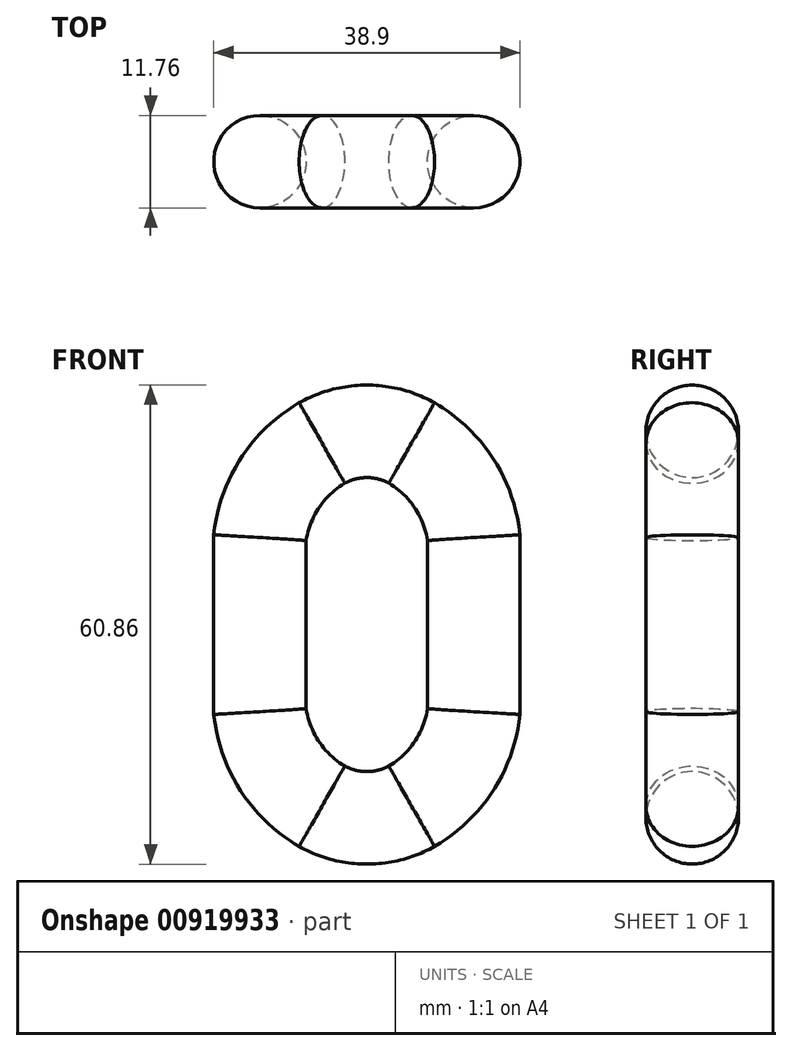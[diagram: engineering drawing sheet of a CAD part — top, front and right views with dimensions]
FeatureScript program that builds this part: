
annotation { "Feature Type Name" : "Feature", "Feature Type Description" : "" }
export const myFeature = defineFeature(function(context is Context, id is Id, definition is map)
    precondition{}
    {
        {
            var Q0;
            Q0=qCreatedBy(makeId("Top.planeOp"),FACE);
            var sketch = newSketch(context, id + "F0", { "sketchPlane" : qUnion([Q0])});
            skCircle(sketch, "E0", {"center": v(13.58, 0) * mm, "radius": 5.88 * mm});
            skSolve(sketch);
        }
        {
            var Q0;
            Q0=qCreatedBy(makeId("Front.planeOp"),FACE);
            var sketch = newSketch(context, id + "F1", { "sketchPlane" : qUnion([Q0])});
            skLineSegment(sketch, "E1", {"start": v(13.58, 0) * mm, "end": v(13.58, 5.5) * mm});
            skArc(sketch, "E2", {"start": v(0, 24.55) * mm, "mid": v(2.94, 24.18) * mm, "end": v(5.7, 23.08) * mm});
            skArc(sketch, "E3", {"start": v(5.7, 23.08) * mm, "mid": v(11.05, 18) * mm, "end": v(13.58, 11.06) * mm});
            skLineSegment(sketch, "E4", {"start": v(13.58, 5.5) * mm, "end": v(13.58, 11.06) * mm});
            skLineSegment(sketch, "E5.MirrorCS", {"start": v(-13.58, 0) * mm, "end": v(-13.58, 5.5) * mm});
            skLineSegment(sketch, "E6.MirrorCS", {"start": v(-13.58, 5.5) * mm, "end": v(-13.58, 11.06) * mm});
            skArc(sketch, "E7.MirrorCS", {"start": v(0, 24.55) * mm, "mid": v(-2.94, 24.18) * mm, "end": v(-5.7, 23.08) * mm});
            skArc(sketch, "E8.MirrorCS", {"start": v(-5.7, 23.08) * mm, "mid": v(-11.05, 18) * mm, "end": v(-13.58, 11.06) * mm});
            skLineSegment(sketch, "E9.MirrorCS", {"start": v(13.58, -5.5) * mm, "end": v(13.58, -11.06) * mm});
            skArc(sketch, "E10.MirrorCS", {"start": v(0, -24.55) * mm, "mid": v(2.94, -24.18) * mm, "end": v(5.7, -23.08) * mm});
            skLineSegment(sketch, "E11.MirrorCS", {"start": v(-13.58, -5.5) * mm, "end": v(-13.58, -11.06) * mm});
            skArc(sketch, "E12.MirrorCS", {"start": v(0, -24.55) * mm, "mid": v(-2.94, -24.18) * mm, "end": v(-5.7, -23.08) * mm});
            skLineSegment(sketch, "E13.MirrorCS", {"start": v(-13.58, 0) * mm, "end": v(-13.58, -5.5) * mm});
            skLineSegment(sketch, "E14.MirrorCS", {"start": v(13.58, 0) * mm, "end": v(13.58, -5.5) * mm});
            skArc(sketch, "E15.MirrorCS", {"start": v(-5.7, -23.08) * mm, "mid": v(-11.05, -18) * mm, "end": v(-13.58, -11.06) * mm});
            skArc(sketch, "E16.MirrorCS", {"start": v(5.7, -23.08) * mm, "mid": v(11.05, -18) * mm, "end": v(13.58, -11.06) * mm});
            skSolve(sketch);
        }
        {
            var Q0;
            Q0=makeQuery(id+"F0.imprint","IMPRINT",FACE,{"disambiguationData":[TD([[makeQuery(id+"F0.imprint","IMPRINT",EDGE,{"derivedFrom":sQuery(id+"F0.wireOp",EDGE,"E0")}),1.0]])]});
            var Q1;
            Q1=sQuery(id+"F1.wireOp",EDGE,"E1");
            var Q2;
            Q2=sQuery(id+"F1.wireOp",EDGE,"E4");
            var Q3;
            Q3=sQuery(id+"F1.wireOp",EDGE,"E3");
            var Q4;
            Q4=sQuery(id+"F1.wireOp",EDGE,"E2");
            var Q5;
            Q5=sQuery(id+"F1.wireOp",EDGE,"E7.MirrorCS");
            var Q6;
            Q6=sQuery(id+"F1.wireOp",EDGE,"E8.MirrorCS");
            var Q7;
            Q7=sQuery(id+"F1.wireOp",EDGE,"E6.MirrorCS");
            var Q8;
            Q8=sQuery(id+"F1.wireOp",EDGE,"E5.MirrorCS");
            var Q9;
            Q9=sQuery(id+"F1.wireOp",EDGE,"E13.MirrorCS");
            var Q10;
            Q10=sQuery(id+"F1.wireOp",EDGE,"E11.MirrorCS");
            var Q11;
            Q11=sQuery(id+"F1.wireOp",EDGE,"E15.MirrorCS");
            var Q12;
            Q12=sQuery(id+"F1.wireOp",EDGE,"E12.MirrorCS");
            var Q13;
            Q13=sQuery(id+"F1.wireOp",EDGE,"E10.MirrorCS");
            var Q14;
            Q14=sQuery(id+"F1.wireOp",EDGE,"E16.MirrorCS");
            var Q15;
            Q15=sQuery(id+"F1.wireOp",EDGE,"E9.MirrorCS");
            var Q16;
            Q16=sQuery(id+"F1.wireOp",EDGE,"E14.MirrorCS");
            sweep(context, id + "F2", {"profiles" : qUnion([Q0]), "path" : qUnion([Q1, Q2, Q3, Q4, Q5, Q6, Q7, Q8, Q9, Q10, Q11, Q12, Q13, Q14, Q15, Q16])});
        }
    });
